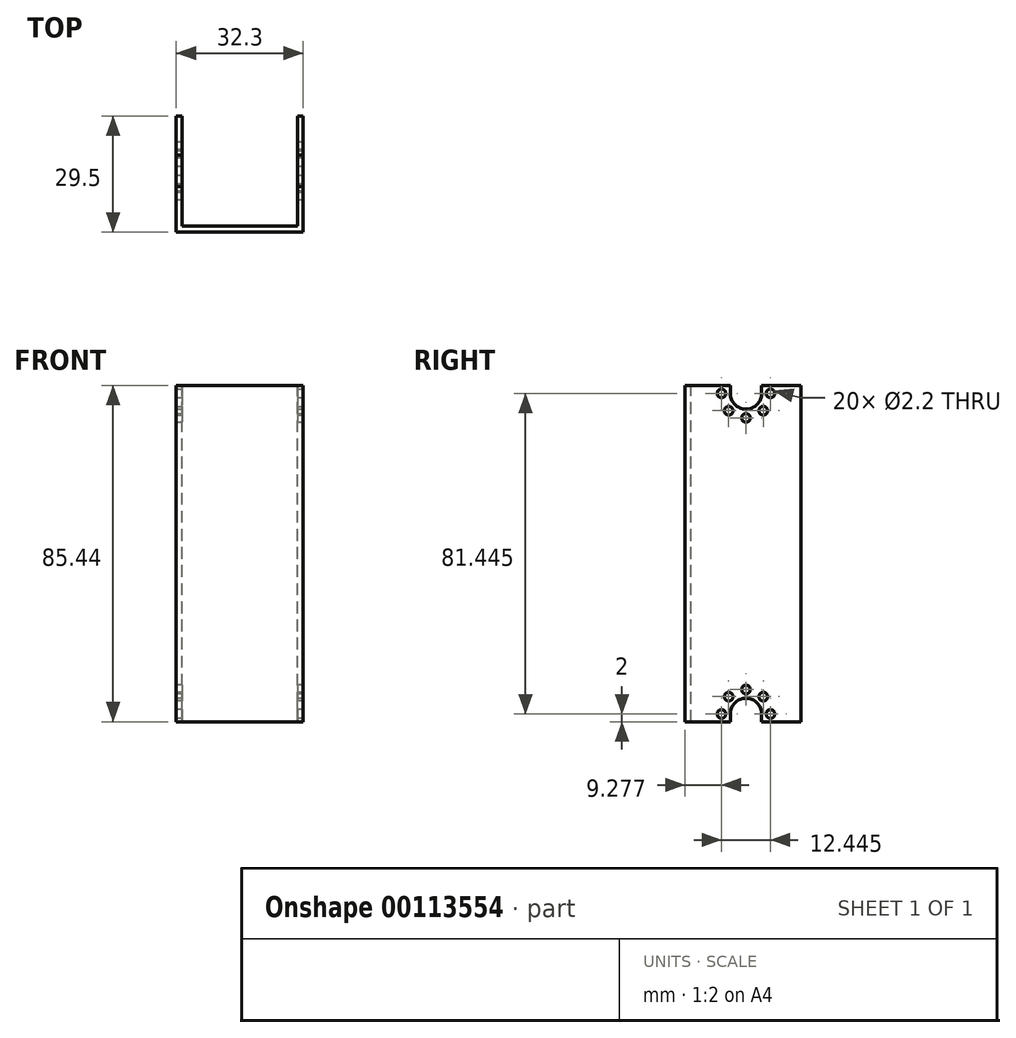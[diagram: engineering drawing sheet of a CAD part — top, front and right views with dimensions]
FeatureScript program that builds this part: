
annotation { "Feature Type Name" : "Feature", "Feature Type Description" : "" }
export const myFeature = defineFeature(function(context is Context, id is Id, definition is map)
    precondition{}
    {
        {
            var Q0;
            Q0=qCreatedBy(makeId("Front.planeOp"),FACE);
            var sketch = newSketch(context, id + "F0", { "sketchPlane" : qUnion([Q0])});
            skLineSegment(sketch, "E0.bottom", {"start": v(0, 0) * mm, "end": v(1.5, 0) * mm});
            skLineSegment(sketch, "E0.top", {"start": v(0, 86.95) * mm, "end": v(32.3, 86.95) * mm});
            skLineSegment(sketch, "E0.left", {"start": v(0, 0) * mm, "end": v(0, 86.95) * mm});
            skLineSegment(sketch, "E0.right", {"start": v(32.3, 0) * mm, "end": v(32.3, 86.95) * mm});
            skLineSegment(sketch, "E1.top", {"start": v(1.5, 85.45) * mm, "end": v(30.8, 85.45) * mm});
            skLineSegment(sketch, "E1.left", {"start": v(1.5, 0) * mm, "end": v(1.5, 85.45) * mm});
            skLineSegment(sketch, "E1.right", {"start": v(30.8, 0) * mm, "end": v(30.8, 85.45) * mm});
            skLineSegment(sketch, "E2.trimOffspring", {"start": v(30.8, 0) * mm, "end": v(32.3, 0) * mm});
            skSolve(sketch);
        }
        {
            var Q0;
            Q0=qSketchRegion(id+"F0",true);
            extrude(context, id + "F1", {"entities" : qUnion([Q0]), "depth" : 28 * mm});
        }
        {
            var Q0;
            Q0=makeQuery(id+"F1.opExtrude","SWEPT_FACE",FACE,{"disambiguationData":[OSD([sQuery(id+"F0.wireOp",EDGE,"E0.left")])]});
            var sketch = newSketch(context, id + "F2", { "sketchPlane" : qUnion([Q0])});
            skArc(sketch, "E3", {"start": v(18, 2) * mm, "mid": v(14, 6) * mm, "end": v(10, 2) * mm});
            skCircle(sketch, "E4", {"center": v(20.22, 2) * mm, "radius": 1.1 * mm});
            skCircle(sketch, "E5.1.0", {"center": v(18.4, 6.4) * mm, "radius": 1.1 * mm});
            skCircle(sketch, "E5.2.0", {"center": v(14, 8.22) * mm, "radius": 1.1 * mm});
            skCircle(sketch, "E5.3.0", {"center": v(9.6, 6.4) * mm, "radius": 1.1 * mm});
            skCircle(sketch, "E5.4.0", {"center": v(7.78, 2) * mm, "radius": 1.1 * mm});
            skLineSegment(sketch, "E6", {"start": v(10, 2) * mm, "end": v(10, 0) * mm});
            skLineSegment(sketch, "E7", {"start": v(18, 2) * mm, "end": v(18, 0) * mm});
            skLineSegment(sketch, "E8", {"start": v(10, 0) * mm, "end": v(18, 0) * mm});
            skLineSegment(sketch, "E9", {"start": v(14, 86.95) * mm, "end": v(14, 0) * mm, "construction": true});
            skPoint(sketch, "E10", {"position": v(14, 0) * mm});
            skLineSegment(sketch, "E11", {"start": v(2.78, 0) * mm, "end": v(0, 0) * mm});
            skLineSegment(sketch, "E12", {"start": v(0, 0) * mm, "end": v(0, 85.45) * mm});
            skLineSegment(sketch, "E13.MirrorCS", {"start": v(28, 0) * mm, "end": v(28, 85.45) * mm});
            skLineSegment(sketch, "E14.MirrorCS", {"start": v(25.22, 0) * mm, "end": v(28, 0) * mm});
            skPoint(sketch, "E15.MirrorCS.end.orphan", {"position": v(28, 85.45) * mm});
            skPoint(sketch, "E15.MirrorCS.start.orphan", {"position": v(25.22, 0) * mm});
            skSolve(sketch);
        }
        {
            var Q0;
            Q0=qSketchRegion(id+"F2",true);
            extrude(context, id + "F3", {"entities" : qUnion([Q0]), "operationType" : NewBodyOperationType.REMOVE, "endBound" : BoundingType.THROUGH_ALL, "oppositeDirection" : true, "depth" : 25 * mm});
        }
        {
            var Q0;
            Q0=makeQuery(id+"F1.opExtrude","SWEPT_FACE",FACE,{"disambiguationData":[OSD([sQuery(id+"F0.wireOp",EDGE,"E0.top")])]});
            var sketch = newSketch(context, id + "F4", { "sketchPlane" : qUnion([Q0])});
            skLineSegment(sketch, "E16", {"start": v(16.15, 0) * mm, "end": v(16.15, -28) * mm, "construction": true});
            skLineSegment(sketch, "E17", {"start": v(0, -14) * mm, "end": v(32.3, -14) * mm, "construction": true});
            skCircle(sketch, "E18", {"center": v(6.15, -4) * mm, "radius": 1.1 * mm});
            skCircle(sketch, "E19.MirrorC", {"center": v(26.15, -4) * mm, "radius": 1.1 * mm});
            skCircle(sketch, "E20.MirrorC", {"center": v(6.15, -24) * mm, "radius": 1.1 * mm});
            skCircle(sketch, "E21.MirrorC", {"center": v(26.15, -24) * mm, "radius": 1.1 * mm});
            skSolve(sketch);
        }
        {
            var Q0;
            Q0=qSketchRegion(id+"F4",true);
            extrude(context, id + "F5", {"entities" : qUnion([Q0]), "operationType" : NewBodyOperationType.REMOVE, "endBound" : BoundingType.UP_TO_NEXT, "oppositeDirection" : true, "depth" : 25 * mm});
        }
        {
            var Q0;
            Q0=makeQuery(id+"F1.opExtrude","SWEPT_FACE",FACE,{"disambiguationData":[OSD([sQuery(id+"F0.wireOp",EDGE,"E0.right")])]});
            var sketch = newSketch(context, id + "F6", { "sketchPlane" : qUnion([Q0])});
            skLineSegment(sketch, "E22.bottom", {"start": v(-28, 86.95) * mm, "end": v(-29.5, 86.95) * mm});
            skLineSegment(sketch, "E22.top", {"start": v(-28, 0) * mm, "end": v(-29.5, 0) * mm});
            skLineSegment(sketch, "E22.left", {"start": v(-28, 86.95) * mm, "end": v(-28, 0) * mm});
            skLineSegment(sketch, "E22.right", {"start": v(-29.5, 86.95) * mm, "end": v(-29.5, 0) * mm});
            skLineSegment(sketch, "E23", {"start": v(-14, 86.95) * mm, "end": v(-14, 0) * mm, "construction": true});
            skLineSegment(sketch, "E24.MirrorCS", {"start": v(0, 86.95) * mm, "end": v(0, 0) * mm});
            skLineSegment(sketch, "E25.MirrorCS", {"start": v(1.5, 86.95) * mm, "end": v(1.5, 0) * mm});
            skLineSegment(sketch, "E26.MirrorCS", {"start": v(0, 86.95) * mm, "end": v(1.5, 86.95) * mm});
            skLineSegment(sketch, "E27.MirrorCS", {"start": v(0, 0) * mm, "end": v(1.5, 0) * mm});
            skSolve(sketch);
        }
        {
            var Q0;
            Q0=makeQuery(id+"F6.imprint","IMPRINT",FACE,{"disambiguationData":[TD([[makeQuery(id+"F6.imprint","IMPRINT",EDGE,{"derivedFrom":sQuery(id+"F6.wireOp",EDGE,"E22.bottom")}),1.0]])]});
            extrude(context, id + "F7", {"entities" : qUnion([Q0]), "operationType" : NewBodyOperationType.ADD, "oppositeDirection" : true, "depth" : 32.3 * mm});
        }
        {
            var Q0;
            Q0=makeQuery(id+"F7.boolean.opBoolean","MERGE",FACE,{"derivedFrom":[makeQuery(id+"F1.opExtrude","SWEPT_FACE",FACE,{"disambiguationData":[OSD([sQuery(id+"F0.wireOp",EDGE,"E0.right")])]}),makeQuery(id+"F7.opExtrude","CAP_FACE",FACE,{"disambiguationData":[OSD([sQuery(id+"F6.wireOp",EDGE,"E22.bottom"),sQuery(id+"F6.wireOp",EDGE,"E22.top"),sQuery(id+"F6.wireOp",EDGE,"E22.left"),sQuery(id+"F6.wireOp",EDGE,"E22.right")])],"isStart":true})]});
            var sketch = newSketch(context, id + "F8", { "sketchPlane" : qUnion([Q0])});
            skLineSegment(sketch, "E28.bottom", {"start": v(-29.5, 86.95) * mm, "end": v(0, 86.95) * mm});
            skLineSegment(sketch, "E28.top", {"start": v(-29.5, 85.45) * mm, "end": v(0, 85.45) * mm});
            skLineSegment(sketch, "E28.left", {"start": v(-29.5, 86.95) * mm, "end": v(-29.5, 85.45) * mm});
            skLineSegment(sketch, "E28.right", {"start": v(0, 86.95) * mm, "end": v(0, 85.45) * mm});
            skLineSegment(sketch, "E29", {"start": v(-29.5, 42.72) * mm, "end": v(0, 42.72) * mm, "construction": true});
            skCircle(sketch, "E30.0", {"center": v(-18.4, 6.4) * mm, "radius": 1.1 * mm});
            skCircle(sketch, "E30.1", {"center": v(-14, 8.22) * mm, "radius": 1.1 * mm});
            skCircle(sketch, "E30.2", {"center": v(-9.6, 6.4) * mm, "radius": 1.1 * mm});
            skArc(sketch, "E30.3", {"start": v(-18, 2) * mm, "mid": v(-14, 6) * mm, "end": v(-10, 2) * mm});
            skCircle(sketch, "E30.4", {"center": v(-7.78, 2) * mm, "radius": 1.1 * mm});
            skCircle(sketch, "E30.5", {"center": v(-20.22, 2) * mm, "radius": 1.1 * mm});
            skLineSegment(sketch, "E30.6", {"start": v(-18, 2) * mm, "end": v(-18, 0) * mm});
            skCircle(sketch, "E30.7", {"center": v(-20.22, 2) * mm, "radius": 1.1 * mm});
            skLineSegment(sketch, "E30.8", {"start": v(-10, 2) * mm, "end": v(-10, 0) * mm});
            skCircle(sketch, "E30.9", {"center": v(-7.78, 2) * mm, "radius": 1.1 * mm});
            skCircle(sketch, "E30.10", {"center": v(-18.4, 6.4) * mm, "radius": 1.1 * mm});
            skArc(sketch, "E30.13", {"start": v(-18, 2) * mm, "mid": v(-14, 6) * mm, "end": v(-10, 2) * mm});
            skCircle(sketch, "E30.14", {"center": v(-14, 8.22) * mm, "radius": 1.1 * mm});
            skCircle(sketch, "E30.15", {"center": v(-20.22, 2) * mm, "radius": 1.1 * mm});
            skLineSegment(sketch, "E30.16", {"start": v(-10, 2) * mm, "end": v(-10, 0) * mm});
            skCircle(sketch, "E30.17", {"center": v(-9.6, 6.4) * mm, "radius": 1.1 * mm});
            skLineSegment(sketch, "E30.20", {"start": v(-18, 2) * mm, "end": v(-18, 0) * mm});
            skCircle(sketch, "E30.21", {"center": v(-14, 8.22) * mm, "radius": 1.1 * mm});
            skArc(sketch, "E30.22", {"start": v(-18, 2) * mm, "mid": v(-14, 6) * mm, "end": v(-10, 2) * mm});
            skCircle(sketch, "E30.23", {"center": v(-9.6, 6.4) * mm, "radius": 1.1 * mm});
            skCircle(sketch, "E30.24", {"center": v(-20.22, 2) * mm, "radius": 1.1 * mm});
            skLineSegment(sketch, "E30.25", {"start": v(-10, 2) * mm, "end": v(-10, 0) * mm});
            skCircle(sketch, "E30.26", {"center": v(-18.4, 6.4) * mm, "radius": 1.1 * mm});
            skCircle(sketch, "E30.27", {"center": v(-7.78, 2) * mm, "radius": 1.1 * mm});
            skLineSegment(sketch, "E30.29", {"start": v(-10, 2) * mm, "end": v(-10, 0) * mm});
            skLineSegment(sketch, "E30.31", {"start": v(-18, 2) * mm, "end": v(-18, 0) * mm});
            skArc(sketch, "E30.33", {"start": v(-18, 2) * mm, "mid": v(-14, 6) * mm, "end": v(-10, 2) * mm});
            skCircle(sketch, "E30.35", {"center": v(-18.4, 6.4) * mm, "radius": 1.1 * mm});
            skCircle(sketch, "E30.36", {"center": v(-14, 8.22) * mm, "radius": 1.1 * mm});
            skCircle(sketch, "E30.37", {"center": v(-9.6, 6.4) * mm, "radius": 1.1 * mm});
            skCircle(sketch, "E30.38", {"center": v(-7.78, 2) * mm, "radius": 1.1 * mm});
            skLineSegment(sketch, "E30.39", {"start": v(-18, 2) * mm, "end": v(-18, 0) * mm});
            skLineSegment(sketch, "E31.MirrorCS", {"start": v(-10, 83.44) * mm, "end": v(-10, 85.44) * mm});
            skLineSegment(sketch, "E32.MirrorCS", {"start": v(-18, 83.44) * mm, "end": v(-18, 85.44) * mm});
            skCircle(sketch, "E33.MirrorC", {"center": v(-9.6, 79.05) * mm, "radius": 1.1 * mm});
            skCircle(sketch, "E34.MirrorC", {"center": v(-18.4, 79.04) * mm, "radius": 1.1 * mm});
            skCircle(sketch, "E35.MirrorC", {"center": v(-7.78, 83.45) * mm, "radius": 1.1 * mm});
            skCircle(sketch, "E36.MirrorC", {"center": v(-14, 77.22) * mm, "radius": 1.1 * mm});
            skCircle(sketch, "E37.MirrorC", {"center": v(-20.22, 83.44) * mm, "radius": 1.1 * mm});
            skArc(sketch, "E38.MirrorCS", {"start": v(-18, 83.44) * mm, "mid": v(-14, 79.44) * mm, "end": v(-10, 83.44) * mm});
            skSolve(sketch);
        }
        {
            var Q0;
            Q0=qSketchRegion(id+"F8",true);
            extrude(context, id + "F9", {"entities" : qUnion([Q0]), "operationType" : NewBodyOperationType.REMOVE, "endBound" : BoundingType.THROUGH_ALL, "oppositeDirection" : true, "depth" : 25 * mm});
        }
    });
